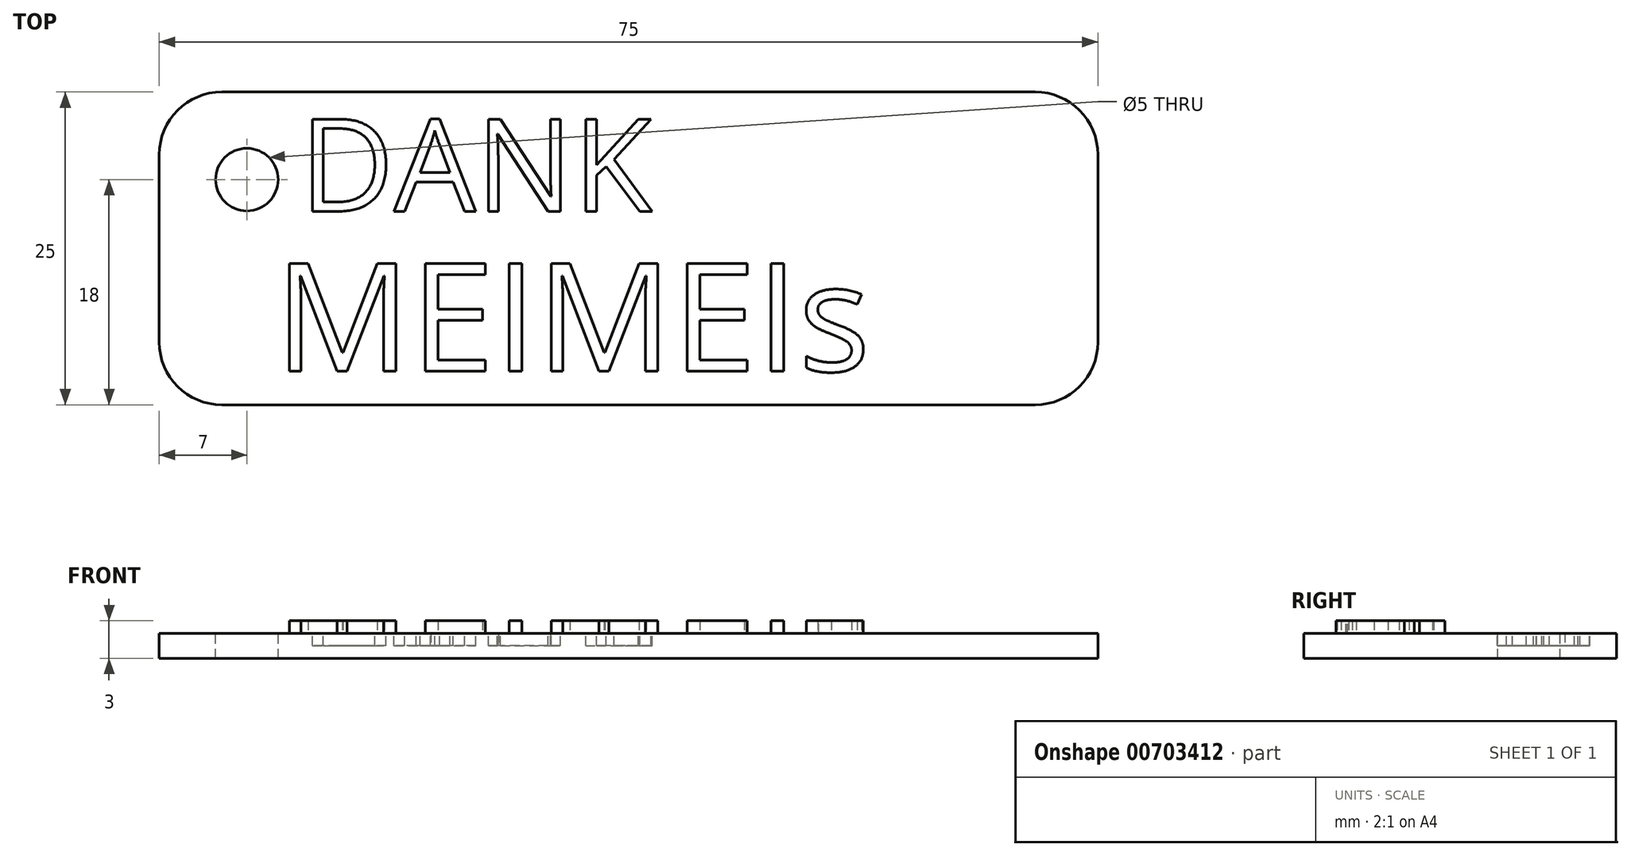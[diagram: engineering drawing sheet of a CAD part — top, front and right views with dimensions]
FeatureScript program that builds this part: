
annotation { "Feature Type Name" : "Feature", "Feature Type Description" : "" }
export const myFeature = defineFeature(function(context is Context, id is Id, definition is map)
    precondition{}
    {
        {
            var Q0;
            Q0=qCreatedBy(makeId("Top.planeOp"),FACE);
            var sketch = newSketch(context, id + "F0", { "sketchPlane" : qUnion([Q0])});
            skLineSegment(sketch, "E0.bottom", {"start": v(-32.5, 12.5) * mm, "end": v(32.5, 12.5) * mm});
            skLineSegment(sketch, "E0.top", {"start": v(-32.5, -12.5) * mm, "end": v(32.5, -12.5) * mm});
            skLineSegment(sketch, "E0.left", {"start": v(-37.5, 7.5) * mm, "end": v(-37.5, -7.5) * mm});
            skLineSegment(sketch, "E0.right", {"start": v(37.5, 7.5) * mm, "end": v(37.5, -7.5) * mm});
            skPoint(sketch, "E0.middle", {"position": v(0, 0) * mm});
            skPoint(sketch, "E1.visualSharp", {"position": v(-37.5, 12.5) * mm});
            skArc(sketch, "E1.filletArc", {"start": v(-32.5, 12.5) * mm, "mid": v(-36.04, 11.04) * mm, "end": v(-37.5, 7.5) * mm});
            skPoint(sketch, "E2.visualSharp", {"position": v(-37.5, -12.5) * mm});
            skArc(sketch, "E2.filletArc", {"start": v(-37.5, -7.5) * mm, "mid": v(-36.04, -11.04) * mm, "end": v(-32.5, -12.5) * mm});
            skPoint(sketch, "E3.visualSharp", {"position": v(37.5, -12.5) * mm});
            skArc(sketch, "E3.filletArc", {"start": v(32.5, -12.5) * mm, "mid": v(36.04, -11.04) * mm, "end": v(37.5, -7.5) * mm});
            skPoint(sketch, "E4.visualSharp", {"position": v(37.5, 12.5) * mm});
            skArc(sketch, "E4.filletArc", {"start": v(37.5, 7.5) * mm, "mid": v(36.04, 11.04) * mm, "end": v(32.5, 12.5) * mm});
            skSolve(sketch);
        }
        {
            var Q0;
            Q0=makeQuery(id+"F0.imprint","IMPRINT",FACE,{"disambiguationData":[TD([[makeQuery(id+"F0.imprint","IMPRINT",EDGE,{"derivedFrom":sQuery(id+"F0.wireOp",EDGE,"E0.bottom")}),-1.0]])]});
            extrude(context, id + "F1", {"entities" : qUnion([Q0]), "depth" : 2 * mm, "offsetDistance" : 25 * mm});
        }
        {
            var Q0;
            Q0=makeQuery(id+"F1.opExtrude","CAP_FACE",FACE,{"disambiguationData":[OSD([sQuery(id+"F0.wireOp",EDGE,"E0.bottom"),sQuery(id+"F0.wireOp",EDGE,"E0.top"),sQuery(id+"F0.wireOp",EDGE,"E0.left"),sQuery(id+"F0.wireOp",EDGE,"E0.right"),sQuery(id+"F0.wireOp",EDGE,"E1.filletArc"),sQuery(id+"F0.wireOp",EDGE,"E2.filletArc"),sQuery(id+"F0.wireOp",EDGE,"E3.filletArc"),sQuery(id+"F0.wireOp",EDGE,"E4.filletArc")])],"isStart":false});
            var sketch = newSketch(context, id + "F2", { "sketchPlane" : qUnion([Q0])});
            skPoint(sketch, "E5", {"position": v(-30.5, 5.5) * mm});
            skPoint(sketch, "E6", {"position": v(-37.5, 7.5) * mm});
            skPoint(sketch, "E7", {"position": v(-32.5, 12.5) * mm});
            skSolve(sketch);
        }
        {
            var Q0;
            Q0=sQuery(id+"F2.wireOp",VERTEX,"E5");
            var Q1;
            Q1=makeQuery(id+"F1.opExtrude","SWEPT_BODY",BODY,{"disambiguationData":[OSD([sQuery(id+"F0.wireOp",EDGE,"E0.bottom"),sQuery(id+"F0.wireOp",EDGE,"E0.top"),sQuery(id+"F0.wireOp",EDGE,"E0.left"),sQuery(id+"F0.wireOp",EDGE,"E0.right"),sQuery(id+"F0.wireOp",EDGE,"E1.filletArc"),sQuery(id+"F0.wireOp",EDGE,"E2.filletArc"),sQuery(id+"F0.wireOp",EDGE,"E3.filletArc"),sQuery(id+"F0.wireOp",EDGE,"E4.filletArc")])]});
            hole(context, id + "F3", {"style" : HoleStyle.SIMPLE, "endStyle" : HoleEndStyle.THROUGH, "holeDiameter" : 5 * mm, "majorDiameter" : 5 * mm, "isTappedThrough" : true, "tappedDepth" : 12 * mm, "tapClearance" : 3, "locations" : qUnion([Q0]), "scope" : qUnion([Q1])});
        }
        {
            var Q0;
            Q0=makeQuery(id+"F1.opExtrude","CAP_FACE",FACE,{"disambiguationData":[OSD([sQuery(id+"F0.wireOp",EDGE,"E0.bottom"),sQuery(id+"F0.wireOp",EDGE,"E0.top"),sQuery(id+"F0.wireOp",EDGE,"E0.left"),sQuery(id+"F0.wireOp",EDGE,"E0.right"),sQuery(id+"F0.wireOp",EDGE,"E1.filletArc"),sQuery(id+"F0.wireOp",EDGE,"E2.filletArc"),sQuery(id+"F0.wireOp",EDGE,"E3.filletArc"),sQuery(id+"F0.wireOp",EDGE,"E4.filletArc")])],"isStart":false});
            var sketch = newSketch(context, id + "F4", { "sketchPlane" : qUnion([Q0])});
            skText(sketch, "E8", { "text": "DANK", "fontName": "OpenSans-Regular.ttf"});
            const initialGuessF4  = {"E8": [-0.02627, 0.00296, 1, 0, 0.00743]};
            skSetInitialGuess(sketch, initialGuessF4);
            skSolve(sketch);
        }
        {
            var Q0;
            Q0 = qSketchRegion(id + "F4", true);
            extrude(context, id + "F5", {"entities" : qUnion([Q0]), "operationType" : NewBodyOperationType.REMOVE, "oppositeDirection" : true, "depth" : 1 * mm, "offsetDistance" : 25 * mm});
        }
        {
            var Q0;
            {var subQ0=sQuery(id+"F0.wireOp",EDGE,"E4.filletArc");var subQ1=sQuery(id+"F0.wireOp",EDGE,"E3.filletArc");var subQ2=sQuery(id+"F0.wireOp",EDGE,"E2.filletArc");var subQ3=sQuery(id+"F0.wireOp",EDGE,"E1.filletArc");var subQ4=sQuery(id+"F0.wireOp",EDGE,"E0.right");var subQ5=sQuery(id+"F0.wireOp",EDGE,"E0.top");var subQ6=sQuery(id+"F0.wireOp",EDGE,"E0.left");var subQ7=sQuery(id+"F0.wireOp",EDGE,"E0.bottom");Q0=makeQuery(id+"F5.boolean.opBoolean","SPLIT",FACE,{"disambiguationData":[TD([makeQuery(id+"F1.opExtrude","SWEPT_FACE",FACE,{"disambiguationData":[OSD([subQ7])]})])],"derivedFrom":makeQuery(id+"F1.opExtrude","CAP_FACE",FACE,{"disambiguationData":[OSD([subQ7,subQ5,subQ6,subQ4,subQ3,subQ2,subQ1,subQ0])],"isStart":false})});}
            var sketch = newSketch(context, id + "F6", { "sketchPlane" : qUnion([Q0])});
            skText(sketch, "E9", { "text": "MEIMEIs", "fontName": "OpenSans-Regular.ttf"});
            const initialGuessF6  = {"E9": [-0.02828, -0.00981, 1, 0, 0.00867]};
            skSetInitialGuess(sketch, initialGuessF6);
            skSolve(sketch);
        }
        {
            var Q0;
            Q0 = qSketchRegion(id + "F6", true);
            extrude(context, id + "F7", {"entities" : qUnion([Q0]), "operationType" : NewBodyOperationType.ADD, "depth" : 1 * mm, "offsetDistance" : 25 * mm});
        }
    });
